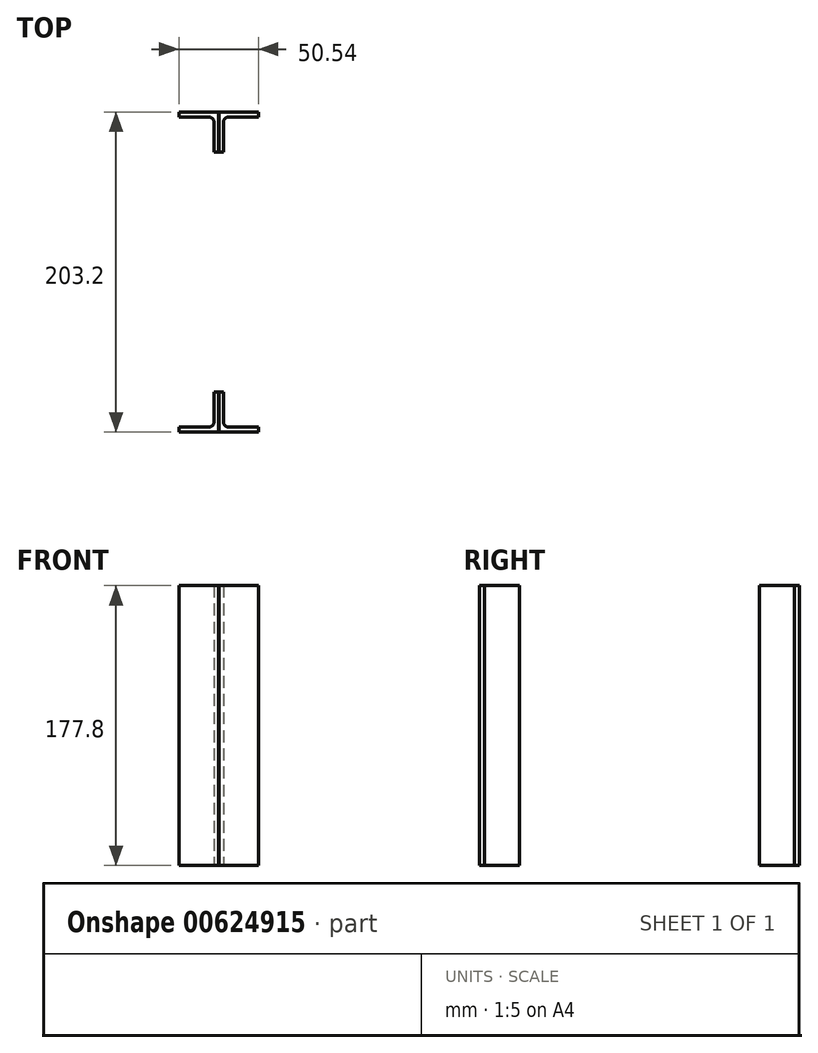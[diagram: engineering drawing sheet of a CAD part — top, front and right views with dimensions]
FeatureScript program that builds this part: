
annotation { "Feature Type Name" : "Feature", "Feature Type Description" : "" }
export const myFeature = defineFeature(function(context is Context, id is Id, definition is map)
    precondition{}
    {
        {
            var Q0;
            Q0=qCreatedBy(makeId("Top.planeOp"),FACE);
            var sketch = newSketch(context, id + "F0", { "sketchPlane" : qUnion([Q0])});
            skLineSegment(sketch, "E0", {"start": v(0, 0) * mm, "end": v(0, -25.4) * mm});
            skLineSegment(sketch, "E1", {"start": v(0, -25.4) * mm, "end": v(3.18, -25.4) * mm});
            skLineSegment(sketch, "E2", {"start": v(3.18, -25.4) * mm, "end": v(3.18, -3.18) * mm});
            skLineSegment(sketch, "E3", {"start": v(3.18, -3.18) * mm, "end": v(25.4, -3.18) * mm});
            skLineSegment(sketch, "E4", {"start": v(25.4, -3.18) * mm, "end": v(25.4, 0) * mm});
            skLineSegment(sketch, "E5", {"start": v(25.4, 0) * mm, "end": v(0, 0) * mm});
            skSolve(sketch);
        }
        {
            var Q0;
            Q0=makeQuery(id+"F0.imprint","IMPRINT",FACE,{"disambiguationData":[TD([[makeQuery(id+"F0.imprint","IMPRINT",EDGE,{"derivedFrom":sQuery(id+"F0.wireOp",EDGE,"E0")}),1.0]])]});
            extrude(context, id + "F1", {"entities" : qUnion([Q0]), "depth" : 177.8 * mm, "offsetDistance" : 25.4 * mm});
        }
        {
            var Q0;
            Q0=qCreatedBy(makeId("Right.planeOp"),FACE);
            cPlane(context, id + "F2", {"entities" : qUnion([Q0]), "cplaneType" : CPlaneType.OFFSET, "offset" : 6.7 / 50.8 * mm, "width" : 152.4 * mm, "height" : 152.4 * mm});
        }
        {
            var Q0;
            Q0=qCreatedBy(makeId("Front.planeOp"),FACE);
            cPlane(context, id + "F3", {"entities" : qUnion([Q0]), "cplaneType" : CPlaneType.OFFSET, "offset" : 101.6 * mm, "width" : 152.4 * mm, "height" : 152.4 * mm});
        }
        {
            var Q0;
            Q0=makeQuery(id+"F1.opExtrude","SWEPT_EDGE",EDGE,{"disambiguationData":[OSD([sQuery(id+"F0.wireOp",EDGE,"E2"),sQuery(id+"F0.wireOp",EDGE,"E3")])]});
            fillet(context, id + "F4", {"entities" : qUnion([Q0]), "radius" : 3.17 * mm, "tangentPropagation" : true, "allowEdgeOverflow" : false});
        }
        {
            var Q0;
            Q0=makeQuery(id+"F1.opExtrude","SWEPT_BODY",BODY,{"disambiguationData":[OSD([sQuery(id+"F0.wireOp",EDGE,"E0"),sQuery(id+"F0.wireOp",EDGE,"E1"),sQuery(id+"F0.wireOp",EDGE,"E2"),sQuery(id+"F0.wireOp",EDGE,"E3"),sQuery(id+"F0.wireOp",EDGE,"E4"),sQuery(id+"F0.wireOp",EDGE,"E5")])]});
            var Q1;
            Q1=qCreatedBy(id+"F3.planeOp",FACE);
            mirror(context, id + "F5", {"entities" : qUnion([Q0]), "mirrorPlane" : qUnion([Q1])});
        }
        {
            var Q0;
            Q0=makeQuery(id+"F1.opExtrude","SWEPT_BODY",BODY,{"disambiguationData":[OSD([sQuery(id+"F0.wireOp",EDGE,"E0"),sQuery(id+"F0.wireOp",EDGE,"E1"),sQuery(id+"F0.wireOp",EDGE,"E2"),sQuery(id+"F0.wireOp",EDGE,"E3"),sQuery(id+"F0.wireOp",EDGE,"E4"),sQuery(id+"F0.wireOp",EDGE,"E5")])]});
            var Q1;
            Q1=makeQuery(id+"F5.opPattern","COPY",BODY,{"derivedFrom":makeQuery(id+"F1.opExtrude","SWEPT_BODY",BODY,{"disambiguationData":[OSD([sQuery(id+"F0.wireOp",EDGE,"E0"),sQuery(id+"F0.wireOp",EDGE,"E1"),sQuery(id+"F0.wireOp",EDGE,"E2"),sQuery(id+"F0.wireOp",EDGE,"E3"),sQuery(id+"F0.wireOp",EDGE,"E4"),sQuery(id+"F0.wireOp",EDGE,"E5")])]}),"instanceName":"1"});
            var Q2;
            Q2=qCreatedBy(id+"F2.planeOp",FACE);
            mirror(context, id + "F6", {"entities" : qUnion([Q0, Q1]), "mirrorPlane" : qUnion([Q2])});
        }
    });
